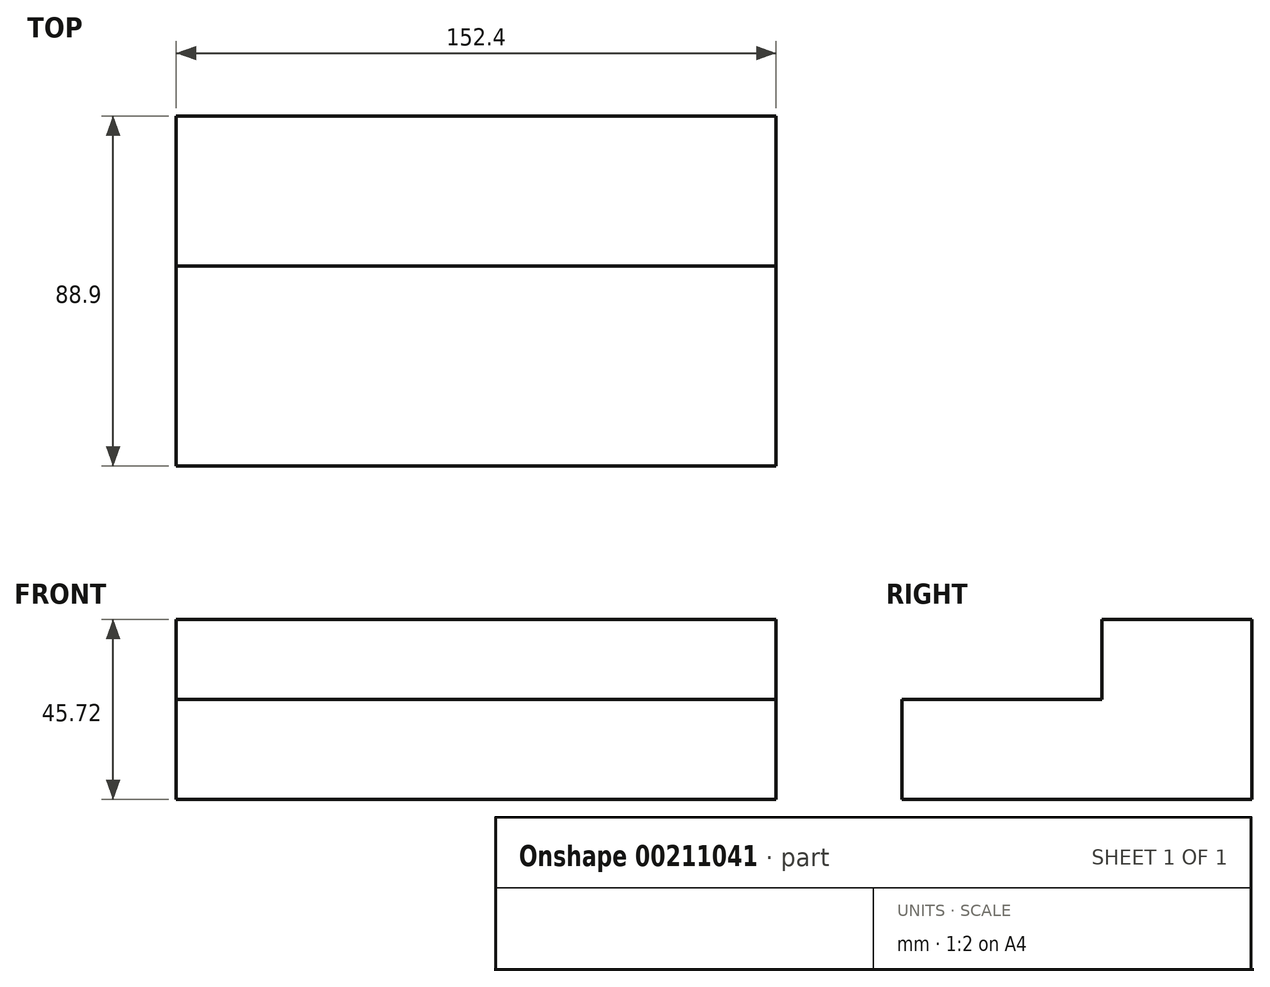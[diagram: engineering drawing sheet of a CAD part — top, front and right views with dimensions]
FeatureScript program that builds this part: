
annotation { "Feature Type Name" : "Feature", "Feature Type Description" : "" }
export const myFeature = defineFeature(function(context is Context, id is Id, definition is map)
    precondition{}
    {
        {
            var Q0;
            Q0=qCreatedBy(makeId("Top.planeOp"),FACE);
            var sketch = newSketch(context, id + "F0", { "sketchPlane" : qUnion([Q0])});
            skLineSegment(sketch, "E0.bottom", {"start": v(-99.13, 15.1) * mm, "end": v(53.27, 15.1) * mm});
            skLineSegment(sketch, "E0.top", {"start": v(-99.13, -23) * mm, "end": v(53.27, -23) * mm});
            skLineSegment(sketch, "E0.left", {"start": v(-99.13, 15.1) * mm, "end": v(-99.13, -23) * mm});
            skLineSegment(sketch, "E0.right", {"start": v(53.27, 15.1) * mm, "end": v(53.27, -23) * mm});
            skSolve(sketch);
        }
        {
            var Q0;
            Q0 = qSketchRegion(id + "F0", true);
            extrude(context, id + "F1", {"entities" : qUnion([Q0]), "depth" : 45.72 * mm});
        }
        {
            var Q0;
            Q0=makeQuery(id+"F1.opExtrude","CAP_FACE",FACE,{"disambiguationData":[OSD([sQuery(id+"F0.wireOp",EDGE,"E0.bottom"),sQuery(id+"F0.wireOp",EDGE,"E0.top"),sQuery(id+"F0.wireOp",EDGE,"E0.left"),sQuery(id+"F0.wireOp",EDGE,"E0.right")])],"isStart":true});
            var sketch = newSketch(context, id + "F2", { "sketchPlane" : qUnion([Q0])});
            skLineSegment(sketch, "E1.bottom", {"start": v(53.27, 23) * mm, "end": v(-99.13, 23) * mm});
            skLineSegment(sketch, "E1.top", {"start": v(53.27, 73.8) * mm, "end": v(-99.13, 73.8) * mm});
            skLineSegment(sketch, "E1.left", {"start": v(53.27, 23) * mm, "end": v(53.27, 73.8) * mm});
            skLineSegment(sketch, "E1.right", {"start": v(-99.13, 23) * mm, "end": v(-99.13, 73.8) * mm});
            skSolve(sketch);
        }
        {
            var Q0;
            Q0 = qSketchRegion(id + "F2", true);
            extrude(context, id + "F3", {"entities" : qUnion([Q0]), "operationType" : NewBodyOperationType.ADD, "oppositeDirection" : true, "depth" : 25.4 * mm});
        }
    });
